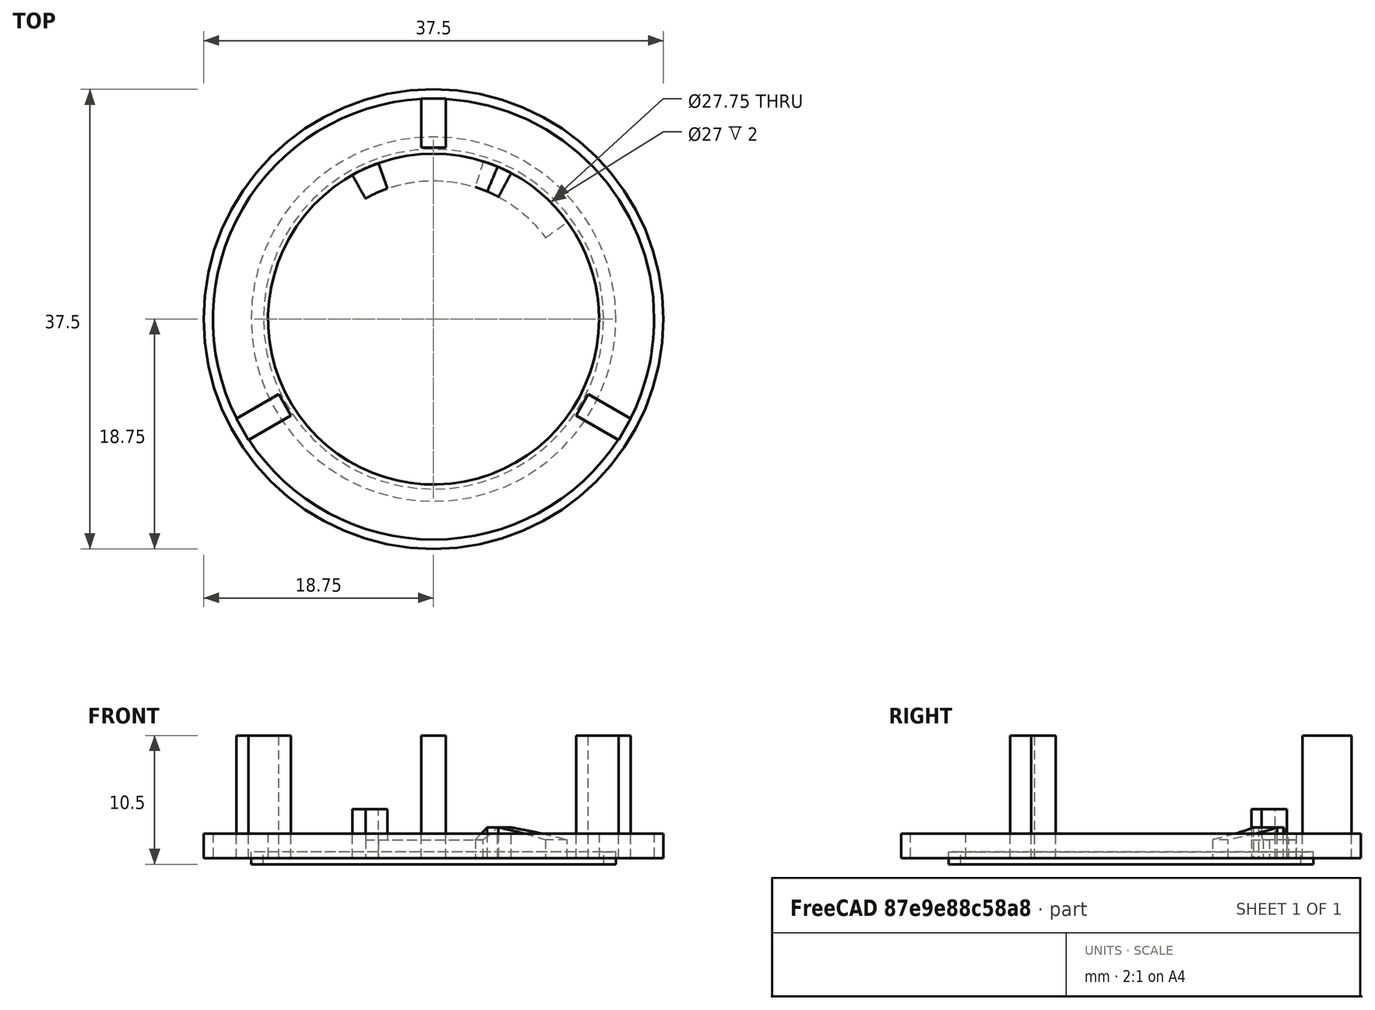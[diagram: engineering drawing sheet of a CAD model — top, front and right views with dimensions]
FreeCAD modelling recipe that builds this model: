
FCSTD DOCUMENT  (FreeCAD 0.19R21857 (Git))
Label: BayonetBaseFemale2
License: All rights reserved
LicenseURL: http://en.wikipedia.org/wiki/All_rights_reserved
objects: Sketcher::SketchObject×28, Part::Sweep×11, Part::MultiFuse×4, Part::Cylinder×3, Part::Mirroring×2, PartDesign::Body×1, Part::Cut×1, Part::Box×1, Part::FeaturePython×1, Image::ImagePlane×1
note: 52 computed .brp shape members not serialized (recipe doc carries the construction recipe); baked Part::Feature solids carry a one-line shape summary decoded from their .brp

FEATURE [Part::Cylinder] Cylinder
  Angle = 360
  AttacherType = Attacher::AttachEngine3D
  Height = 2
  Radius = 18.75
FEATURE [Sketcher::SketchObject] Sketch  label="RampStart"
  Placement = pos=(0,0,0) rot=(1,0,0;1.5708rad)
  sketch-geometry (4):
    g0: LineSegment StartX=-13.5 StartY=0 StartZ=0 EndX=-13.5 EndY=1.5 EndZ=0
    g1: LineSegment StartX=-13.5 StartY=1.5 StartZ=0 EndX=-11.3 EndY=1.5 EndZ=0
    g2: LineSegment StartX=-11.3 StartY=1.5 StartZ=0 EndX=-11.3 EndY=0 EndZ=0
    g3: LineSegment StartX=-11.3 StartY=0 StartZ=0 EndX=-13.5 EndY=0 EndZ=0
  constraints (12):
    c: Coincident(g0,g1)
    c: Coincident(g1,g2)
    c: Coincident(g2,g3)
    c: Coincident(g3,g0)
    c: Parallel(g0,g2)
    c: Parallel(g1,g3)
    c: Horizontal(g3)
    c: Vertical(g2)
    c: DistanceY(g-1,g2) = 0
    c: DistanceX(g2,g-1) = 11.3
    c: DistanceX(g0,g-1) = 13.5
    c: DistanceY(g0,g0) = 1.5
FEATURE [Sketcher::SketchObject] Sketch001  label="InnerCircumference"
  Placement = pos=(0,0,0) rot=(1,0,0;3.14159rad)
  sketch-geometry (1):
    g0: Circle CenterX=0 CenterY=0 CenterZ=0 NormalX=0 NormalY=0 NormalZ=1 AngleXU=0 Radius=11
  constraints (1):
    c: Radius(g0) = 11
FEATURE [Sketcher::SketchObject] Sketch002  label="RampEnd"
  Placement = pos=(0,0,0) rot=(0.950615,-0.219467,-0.219467;1.62142rad)
  sketch-geometry (4):
    g0: LineSegment StartX=-13.5 StartY=0 StartZ=0 EndX=-13.5 EndY=2.5 EndZ=0
    g1: LineSegment StartX=-13.5 StartY=2.5 StartZ=0 EndX=-11.3 EndY=2.5 EndZ=0
    g2: LineSegment StartX=-11.3 StartY=2.5 StartZ=0 EndX=-11.3 EndY=0 EndZ=0
    g3: LineSegment StartX=-11.3 StartY=0 StartZ=0 EndX=-13.5 EndY=0 EndZ=0
  constraints (12):
    c: Coincident(g0,g1)
    c: Coincident(g1,g2)
    c: Coincident(g2,g3)
    c: Coincident(g3,g0)
    c: Parallel(g0,g2)
    c: Parallel(g1,g3)
    c: Horizontal(g3)
    c: Vertical(g2)
    c: DistanceY(g-1,g2) = 0
    c: DistanceX(g2,g-1) = 11.3
    c: DistanceX(g0,g-1) = 13.5
    c: DistanceY(g0,g0) = 2.5
FEATURE [Sketcher::SketchObject] Sketch003  label="RampFlat"
  Placement = pos=(0,0,0) rot=(0.930118,-0.259693,-0.259693;1.64318rad)
  sketch-geometry (4):
    g0: LineSegment StartX=-13.5 StartY=0 StartZ=0 EndX=-13.5 EndY=2.5 EndZ=0
    g1: LineSegment StartX=-13.5 StartY=2.5 StartZ=0 EndX=-11.3 EndY=2.5 EndZ=0
    g2: LineSegment StartX=-11.3 StartY=2.5 StartZ=0 EndX=-11.3 EndY=0 EndZ=0
    g3: LineSegment StartX=-11.3 StartY=0 StartZ=0 EndX=-13.5 EndY=0 EndZ=0
  constraints (12):
    c: Coincident(g0,g1)
    c: Coincident(g1,g2)
    c: Coincident(g2,g3)
    c: Coincident(g3,g0)
    c: Parallel(g0,g2)
    c: Parallel(g1,g3)
    c: Horizontal(g3)
    c: Vertical(g2)
    c: DistanceY(g-1,g2) = 0
    c: DistanceX(g2,g-1) = 11.3
    c: DistanceX(g0,g-1) = 13.5
    c: DistanceY(g0,g0) = 2.5
FEATURE [Sketcher::SketchObject] Sketch004  label="LockFlat"
  Placement = pos=(0,0,0) rot=(0.906297,-0.298852,-0.298852;1.66903rad)
  sketch-geometry (4):
    g0: LineSegment StartX=-13.5 StartY=0 StartZ=0 EndX=-13.5 EndY=1.5 EndZ=0
    g1: LineSegment StartX=-13.5 StartY=1.5 StartZ=0 EndX=-11.3 EndY=1.5 EndZ=0
    g2: LineSegment StartX=-11.3 StartY=1.5 StartZ=0 EndX=-11.3 EndY=0 EndZ=0
    g3: LineSegment StartX=-11.3 StartY=0 StartZ=0 EndX=-13.5 EndY=0 EndZ=0
  constraints (12):
    c: Coincident(g0,g1)
    c: Coincident(g1,g2)
    c: Coincident(g2,g3)
    c: Coincident(g3,g0)
    c: Parallel(g0,g2)
    c: Parallel(g1,g3)
    c: Horizontal(g3)
    c: Vertical(g2)
    c: DistanceY(g-1,g2) = 0
    c: DistanceX(g2,g-1) = 11.3
    c: DistanceX(g0,g-1) = 13.5
    c: DistanceY(g0,g0) = 1.5
FEATURE [Sketcher::SketchObject] Sketch005  label="LockFlatEnd"
  Placement = pos=(0,0,0) rot=(0.621652,-0.553872,-0.553872;2.02922rad)
  sketch-geometry (4):
    g0: LineSegment StartX=-13.5 StartY=0 StartZ=0 EndX=-13.5 EndY=1.5 EndZ=0
    g1: LineSegment StartX=-13.5 StartY=1.5 StartZ=0 EndX=-11.3 EndY=1.5 EndZ=0
    g2: LineSegment StartX=-11.3 StartY=1.5 StartZ=0 EndX=-11.3 EndY=0 EndZ=0
    g3: LineSegment StartX=-11.3 StartY=0 StartZ=0 EndX=-13.5 EndY=0 EndZ=0
  constraints (12):
    c: Coincident(g0,g1)
    c: Coincident(g1,g2)
    c: Coincident(g2,g3)
    c: Coincident(g3,g0)
    c: Parallel(g0,g2)
    c: Parallel(g1,g3)
    c: Horizontal(g3)
    c: Vertical(g2)
    c: DistanceY(g-1,g2) = 0
    c: DistanceX(g2,g-1) = 11.3
    c: DistanceX(g0,g-1) = 13.5
    c: DistanceY(g0,g0) = 1.5
FEATURE [Sketcher::SketchObject] Sketch006  label="RampPath"
  sketch-geometry (1):
    g0: ArcOfCircle CenterX=0 CenterY=0 CenterZ=0 NormalX=0 NormalY=0 NormalZ=1 AngleXU=0 Radius=11.0109 StartAngle=1.68589 EndAngle=3.14182
FEATURE [Sketcher::SketchObject] Sketch007  label="Path1"
  sketch-geometry (2):
    g0: ArcOfCircle CenterX=0 CenterY=0 CenterZ=0 NormalX=0 NormalY=0 NormalZ=1 AngleXU=0 Radius=11.3 StartAngle=2.68754 EndAngle=3.14132
    g1: GeomPoint X=-10.1564 Y=4.95359 Z=0
  constraints (3):
    c: Radius(g0) = 11.3
    c: Coincident(g-1,g0)
    c: Angle(g0) = 0.453786
FEATURE [PartDesign::Body] Body
  Group = -> [Sketch005,Sketch004,Sketch003,Sketch002,Sketch001,Sketch,Sketch006,Sketch007]
  Origin = -> Origin
FEATURE [Part::Sweep] Sweep
  Frenet = false
  Sections = -> [Sketch,Sketch002]
  Solid = true
  Spine = -> Sketch007 [Edge1]
  Transition = 1
FEATURE [Sketcher::SketchObject] Sketch008  label="Path2"
  sketch-geometry (1):
    g0: ArcOfCircle CenterX=0 CenterY=0 CenterZ=0 NormalX=0 NormalY=0 NormalZ=1 AngleXU=0 Radius=11.3 StartAngle=2.59707 EndAngle=2.68754
  constraints (2):
    c: Radius(g0) = 11.3
    c: Coincident(g0,g-1)
FEATURE [Sketcher::SketchObject] Sketch009  label="Path3"
  sketch-geometry (1):
    g0: ArcOfCircle CenterX=0 CenterY=0 CenterZ=0 NormalX=0 NormalY=0 NormalZ=1 AngleXU=0 Radius=11.3 StartAngle=2.50468 EndAngle=2.59704
  constraints (2):
    c: Radius(g0) = 11.3
    c: Coincident(g0,g-1)
FEATURE [Sketcher::SketchObject] Sketch010  label="Path4"
  sketch-geometry (1):
    g0: ArcOfCircle CenterX=0 CenterY=0 CenterZ=0 NormalX=0 NormalY=0 NormalZ=1 AngleXU=0 Radius=11.3 StartAngle=1.68594 EndAngle=2.50452
  constraints (2):
    c: Radius(g0) = 11.3
    c: Coincident(g0,g-1)
FEATURE [Part::Sweep] Sweep001
  Frenet = false
  Sections = -> [Sketch002,Sketch003]
  Solid = true
  Spine = -> Sketch008 [Edge1]
  Transition = 1
FEATURE [Part::Sweep] Sweep002
  Frenet = false
  Sections = -> [Sketch003,Sketch004]
  Solid = true
  Spine = -> Sketch009 [Edge1]
  Transition = 1
FEATURE [Part::Sweep] Sweep003
  Frenet = false
  Sections = -> [Sketch004,Sketch005]
  Solid = true
  Spine = -> Sketch010 [Edge1]
  Transition = 1
FEATURE [Part::MultiFuse] Fusion  label="Ramp"
  Shapes = -> [Sweep,Sweep001,Sweep002,Sweep003]
FEATURE [Sketcher::SketchObject] Sketch011  label="EndstopEnd"
  Placement = pos=(0,0,0) rot=(0.621652,-0.553872,-0.553872;2.02922rad)
  sketch-geometry (4):
    g0: LineSegment StartX=-13.5 StartY=0 StartZ=0 EndX=-13.5 EndY=4 EndZ=0
    g1: LineSegment StartX=-13.5 StartY=4 StartZ=0 EndX=-11.3 EndY=4 EndZ=0
    g2: LineSegment StartX=-11.3 StartY=4 StartZ=0 EndX=-11.3 EndY=0 EndZ=0
    g3: LineSegment StartX=-11.3 StartY=0 StartZ=0 EndX=-13.5 EndY=0 EndZ=0
  constraints (12):
    c: Coincident(g0,g1)
    c: Coincident(g1,g2)
    c: Coincident(g2,g3)
    c: Coincident(g3,g0)
    c: Parallel(g0,g2)
    c: Parallel(g1,g3)
    c: Horizontal(g3)
    c: Vertical(g2)
    c: DistanceY(g-1,g2) = 0
    c: DistanceX(g2,g-1) = 11.3
    c: DistanceX(g0,g-1) = 13.5
    c: DistanceY(g0,g0) = 4
FEATURE [Sketcher::SketchObject] Sketch012  label="EndstopStart"
  Placement = pos=(0,0,0) rot=(0.688237,-0.512996,-0.512996;1.93602rad)
  sketch-geometry (4):
    g0: LineSegment StartX=-13.5 StartY=0 StartZ=0 EndX=-13.5 EndY=4 EndZ=0
    g1: LineSegment StartX=-13.5 StartY=4 StartZ=0 EndX=-11.3 EndY=4 EndZ=0
    g2: LineSegment StartX=-11.3 StartY=4 StartZ=0 EndX=-11.3 EndY=0 EndZ=0
    g3: LineSegment StartX=-11.3 StartY=0 StartZ=0 EndX=-13.5 EndY=0 EndZ=0
  constraints (12):
    c: Coincident(g0,g1)
    c: Coincident(g1,g2)
    c: Coincident(g2,g3)
    c: Coincident(g3,g0)
    c: Parallel(g0,g2)
    c: Parallel(g1,g3)
    c: Horizontal(g3)
    c: Vertical(g2)
    c: DistanceY(g-1,g2) = 0
    c: DistanceX(g2,g-1) = 11.3
    c: DistanceX(g0,g-1) = 13.5
    c: DistanceY(g0,g0) = 4
FEATURE [Sketcher::SketchObject] Sketch013  label="EndstopPath"
  sketch-geometry (1):
    g0: ArcOfCircle CenterX=0 CenterY=0 CenterZ=0 NormalX=0 NormalY=0 NormalZ=1 AngleXU=0 Radius=11.3 StartAngle=1.68607 EndAngle=1.86043
  constraints (2):
    c: Radius(g0) = 11.3
    c: Coincident(g-1,g0)
FEATURE [Part::Sweep] Sweep004  label="EndStop"
  Frenet = false
  Sections = -> [Sketch012,Sketch011]
  Solid = true
  Spine = -> Sketch013 [Edge1]
  Transition = 1
FEATURE [Part::MultiFuse] Fusion001  label="RampWithEndstop"
  Shapes = -> [Fusion,Sweep004]
FEATURE [Part::Cylinder] Cylinder001
  Angle = 360
  AttacherType = Attacher::AttachEngine3D
  Height = 2
  Radius = 18
FEATURE [Part::Cylinder] Cylinder002
  Angle = 360
  AttacherType = Attacher::AttachEngine3D
  Height = 2
  Radius = 13.5
FEATURE [Part::Cut] Cut  label="Base"
  Base = -> Cylinder001
  Placement = pos=(0,0,2) rot=(1,0,0;3.14159rad)
  Tool = -> Cylinder002
FEATURE [Sketcher::SketchObject] Sketch015  label="GrooveProfile"
  Placement = pos=(0,0,0) rot=(1,0,0;1.5708rad)
  sketch-geometry (4):
    g0: LineSegment StartX=-14.875 StartY=-0.5 StartZ=0 EndX=-13.875 EndY=-0.5 EndZ=0
    g1: LineSegment StartX=-13.875 StartY=-0.5 StartZ=0 EndX=-13.875 EndY=0.5 EndZ=0
    g2: LineSegment StartX=-13.875 StartY=0.5 StartZ=0 EndX=-14.875 EndY=0.5 EndZ=0
    g3: LineSegment StartX=-14.875 StartY=0.5 StartZ=0 EndX=-14.875 EndY=-0.5 EndZ=0
  constraints (12):
    c: Coincident(g0,g1)
    c: Coincident(g1,g2)
    c: Coincident(g2,g3)
    c: Coincident(g3,g0)
    c: Horizontal(g0)
    c: Horizontal(g2)
    c: Vertical(g1)
    c: Vertical(g3)
    c: DistanceX(g0,g0) = 1
    c: Equal(g0,g1)
    c: DistanceY(g1,g-1) = -0.5
    c: DistanceX(g1,g-1) = 13.875
FEATURE [Sketcher::SketchObject] Sketch016  label="GroovePath"
  sketch-geometry (1):
    g0: Circle CenterX=0 CenterY=0 CenterZ=0 NormalX=0 NormalY=0 NormalZ=1 AngleXU=0 Radius=13.875
  constraints (2):
    c: Coincident(g0,g-1)
    c: Radius(g0) = 13.875
FEATURE [Part::Sweep] Sweep005  label="Groove"
  Frenet = false
  Sections = -> [Sketch015]
  Solid = true
  Spine = -> Sketch016 [Edge1]
  Transition = 1
FEATURE [Part::Box] Box  label="Cube"
  AttacherType = Attacher::AttachEngine3D
  Height = 10
  Length = 2
  Placement = pos=(-1,14,0) rot=(0,0,1;0rad)
  Width = 4
FEATURE [Part::FeaturePython] Array001  label="Testhandles"  # Draft array (typed FeaturePython)
  Angle = 360
  ArrayType = 1
  Axis = (0,0,1)
  Base = -> Box
  Center = (0,0,0)
  Fuse = false
  IntervalAxis = (0,0,0)
  IntervalX = (1,0,0)
  IntervalY = (0,1,0)
  IntervalZ = (0,0,1)
  NumberPolar = 3
  NumberX = 0
  NumberY = 0
  NumberZ = 0
FEATURE [Part::Mirroring] Part__Mirroring  label="RampWithEndstop (Mirror #1)"
  Base = (0,0,0)
  Normal = (0,1,0)
  Placement = pos=(0,0,0) rot=(0,0,-1;2.51327rad)
  Source = -> Fusion001
FEATURE [Image::ImagePlane] ImagePlane
  Placement = pos=(0.5,6,2) rot=(0,1,0;3.14159rad)
  XSize = 50.7829
  YSize = 59.8109
FEATURE [Sketcher::SketchObject] Sketch017  label="RampEnd001"
  Placement = pos=(0,0,0) rot=(0.950615,-0.219467,-0.219467;1.62142rad)
  sketch-geometry (4):
    g0: LineSegment StartX=-13.5 StartY=0 StartZ=0 EndX=-13.5 EndY=2.5 EndZ=0
    g1: LineSegment StartX=-13.5 StartY=2.5 StartZ=0 EndX=-11.3 EndY=2.5 EndZ=0
    g2: LineSegment StartX=-11.3 StartY=2.5 StartZ=0 EndX=-11.3 EndY=0 EndZ=0
    g3: LineSegment StartX=-11.3 StartY=0 StartZ=0 EndX=-13.5 EndY=0 EndZ=0
  constraints (12):
    c: Coincident(g0,g1)
    c: Coincident(g1,g2)
    c: Coincident(g2,g3)
    c: Coincident(g3,g0)
    c: Parallel(g0,g2)
    c: Parallel(g1,g3)
    c: Horizontal(g3)
    c: Vertical(g2)
    c: DistanceY(g-1,g2) = 0
    c: DistanceX(g2,g-1) = 11.3
    c: DistanceX(g0,g-1) = 13.5
    c: DistanceY(g0,g0) = 2.5
FEATURE [Sketcher::SketchObject] Sketch018  label="RampFlat001"
  Placement = pos=(0,0,0) rot=(0.930118,-0.259693,-0.259693;1.64318rad)
  sketch-geometry (4):
    g0: LineSegment StartX=-13.5 StartY=0 StartZ=0 EndX=-13.5 EndY=2.5 EndZ=0
    g1: LineSegment StartX=-13.5 StartY=2.5 StartZ=0 EndX=-11.3 EndY=2.5 EndZ=0
    g2: LineSegment StartX=-11.3 StartY=2.5 StartZ=0 EndX=-11.3 EndY=0 EndZ=0
    g3: LineSegment StartX=-11.3 StartY=0 StartZ=0 EndX=-13.5 EndY=0 EndZ=0
  constraints (12):
    c: Coincident(g0,g1)
    c: Coincident(g1,g2)
    c: Coincident(g2,g3)
    c: Coincident(g3,g0)
    c: Parallel(g0,g2)
    c: Parallel(g1,g3)
    c: Horizontal(g3)
    c: Vertical(g2)
    c: DistanceY(g-1,g2) = 0
    c: DistanceX(g2,g-1) = 11.3
    c: DistanceX(g0,g-1) = 13.5
    c: DistanceY(g0,g0) = 2.5
FEATURE [Sketcher::SketchObject] Sketch019  label="LockFlat001"
  Placement = pos=(0,0,0) rot=(0.906297,-0.298852,-0.298852;1.66903rad)
  sketch-geometry (4):
    g0: LineSegment StartX=-13.5 StartY=0 StartZ=0 EndX=-13.5 EndY=1.5 EndZ=0
    g1: LineSegment StartX=-13.5 StartY=1.5 StartZ=0 EndX=-11.3 EndY=1.5 EndZ=0
    g2: LineSegment StartX=-11.3 StartY=1.5 StartZ=0 EndX=-11.3 EndY=0 EndZ=0
    g3: LineSegment StartX=-11.3 StartY=0 StartZ=0 EndX=-13.5 EndY=0 EndZ=0
  constraints (12):
    c: Coincident(g0,g1)
    c: Coincident(g1,g2)
    c: Coincident(g2,g3)
    c: Coincident(g3,g0)
    c: Parallel(g0,g2)
    c: Parallel(g1,g3)
    c: Horizontal(g3)
    c: Vertical(g2)
    c: DistanceY(g-1,g2) = 0
    c: DistanceX(g2,g-1) = 11.3
    c: DistanceX(g0,g-1) = 13.5
    c: DistanceY(g0,g0) = 1.5
FEATURE [Sketcher::SketchObject] Sketch020  label="LockFlatEnd001"
  Placement = pos=(0,0,0) rot=(0.621652,-0.553872,-0.553872;2.02922rad)
  sketch-geometry (4):
    g0: LineSegment StartX=-13.5 StartY=0 StartZ=0 EndX=-13.5 EndY=1.5 EndZ=0
    g1: LineSegment StartX=-13.5 StartY=1.5 StartZ=0 EndX=-11.3 EndY=1.5 EndZ=0
    g2: LineSegment StartX=-11.3 StartY=1.5 StartZ=0 EndX=-11.3 EndY=0 EndZ=0
    g3: LineSegment StartX=-11.3 StartY=0 StartZ=0 EndX=-13.5 EndY=0 EndZ=0
  constraints (12):
    c: Coincident(g0,g1)
    c: Coincident(g1,g2)
    c: Coincident(g2,g3)
    c: Coincident(g3,g0)
    c: Parallel(g0,g2)
    c: Parallel(g1,g3)
    c: Horizontal(g3)
    c: Vertical(g2)
    c: DistanceY(g-1,g2) = 0
    c: DistanceX(g2,g-1) = 11.3
    c: DistanceX(g0,g-1) = 13.5
    c: DistanceY(g0,g0) = 1.5
FEATURE [Sketcher::SketchObject] Sketch021  label="Path005"
  sketch-geometry (2):
    g0: ArcOfCircle CenterX=0 CenterY=0 CenterZ=0 NormalX=0 NormalY=0 NormalZ=1 AngleXU=0 Radius=11.3 StartAngle=2.68754 EndAngle=3.14132
    g1: GeomPoint X=-10.1564 Y=4.95359 Z=0
  constraints (3):
    c: Radius(g0) = 11.3
    c: Coincident(g-1,g0)
    c: Angle(g0) = 0.453786
FEATURE [Sketcher::SketchObject] Sketch022  label="Path006"
  sketch-geometry (1):
    g0: ArcOfCircle CenterX=0 CenterY=0 CenterZ=0 NormalX=0 NormalY=0 NormalZ=1 AngleXU=0 Radius=11.3 StartAngle=2.59707 EndAngle=2.68754
  constraints (2):
    c: Radius(g0) = 11.3
    c: Coincident(g0,g-1)
FEATURE [Part::Sweep] Sweep007
  Frenet = false
  Sections = -> [Sketch017,Sketch018]
  Solid = true
  Spine = -> Sketch022 [Edge1]
  Transition = 1
FEATURE [Sketcher::SketchObject] Sketch023  label="Path007"
  sketch-geometry (1):
    g0: ArcOfCircle CenterX=0 CenterY=0 CenterZ=0 NormalX=0 NormalY=0 NormalZ=1 AngleXU=0 Radius=11.3 StartAngle=2.50468 EndAngle=2.59704
  constraints (2):
    c: Radius(g0) = 11.3
    c: Coincident(g0,g-1)
FEATURE [Part::Sweep] Sweep006
  Frenet = false
  Sections = -> [Sketch018,Sketch019]
  Solid = true
  Spine = -> Sketch023 [Edge1]
  Transition = 1
FEATURE [Sketcher::SketchObject] Sketch024  label="Path008"
  sketch-geometry (1):
    g0: ArcOfCircle CenterX=0 CenterY=0 CenterZ=0 NormalX=0 NormalY=0 NormalZ=1 AngleXU=0 Radius=11.3 StartAngle=1.68594 EndAngle=2.50452
  constraints (2):
    c: Radius(g0) = 11.3
    c: Coincident(g0,g-1)
FEATURE [Sketcher::SketchObject] Sketch025  label="EndstopEnd001"
  Placement = pos=(0,0,0) rot=(0.621652,-0.553872,-0.553872;2.02922rad)
  sketch-geometry (4):
    g0: LineSegment StartX=-13.5 StartY=0 StartZ=0 EndX=-13.5 EndY=4 EndZ=0
    g1: LineSegment StartX=-13.5 StartY=4 StartZ=0 EndX=-11.3 EndY=4 EndZ=0
    g2: LineSegment StartX=-11.3 StartY=4 StartZ=0 EndX=-11.3 EndY=0 EndZ=0
    g3: LineSegment StartX=-11.3 StartY=0 StartZ=0 EndX=-13.5 EndY=0 EndZ=0
  constraints (12):
    c: Coincident(g0,g1)
    c: Coincident(g1,g2)
    c: Coincident(g2,g3)
    c: Coincident(g3,g0)
    c: Parallel(g0,g2)
    c: Parallel(g1,g3)
    c: Horizontal(g3)
    c: Vertical(g2)
    c: DistanceY(g-1,g2) = 0
    c: DistanceX(g2,g-1) = 11.3
    c: DistanceX(g0,g-1) = 13.5
    c: DistanceY(g0,g0) = 4
FEATURE [Sketcher::SketchObject] Sketch026  label="EndstopStart001"
  Placement = pos=(0,0,0) rot=(0.688237,-0.512996,-0.512996;1.93602rad)
  sketch-geometry (4):
    g0: LineSegment StartX=-13.5 StartY=0 StartZ=0 EndX=-13.5 EndY=4 EndZ=0
    g1: LineSegment StartX=-13.5 StartY=4 StartZ=0 EndX=-11.3 EndY=4 EndZ=0
    g2: LineSegment StartX=-11.3 StartY=4 StartZ=0 EndX=-11.3 EndY=0 EndZ=0
    g3: LineSegment StartX=-11.3 StartY=0 StartZ=0 EndX=-13.5 EndY=0 EndZ=0
  constraints (12):
    c: Coincident(g0,g1)
    c: Coincident(g1,g2)
    c: Coincident(g2,g3)
    c: Coincident(g3,g0)
    c: Parallel(g0,g2)
    c: Parallel(g1,g3)
    c: Horizontal(g3)
    c: Vertical(g2)
    c: DistanceY(g-1,g2) = 0
    c: DistanceX(g2,g-1) = 11.3
    c: DistanceX(g0,g-1) = 13.5
    c: DistanceY(g0,g0) = 4
FEATURE [Sketcher::SketchObject] Sketch027  label="EndstopPath001"
  sketch-geometry (1):
    g0: ArcOfCircle CenterX=0 CenterY=0 CenterZ=0 NormalX=0 NormalY=0 NormalZ=1 AngleXU=0 Radius=11.3 StartAngle=1.68607 EndAngle=1.86043
  constraints (2):
    c: Radius(g0) = 11.3
    c: Coincident(g-1,g0)
FEATURE [Part::Sweep] Sweep009  label="EndStop001"
  Frenet = false
  Sections = -> [Sketch026,Sketch025]
  Solid = true
  Spine = -> Sketch027 [Edge1]
  Transition = 1
FEATURE [Part::Sweep] Sweep010
  Frenet = false
  Sections = -> [Sketch019,Sketch020]
  Solid = true
  Spine = -> Sketch024 [Edge1]
  Transition = 1
FEATURE [Sketcher::SketchObject] Sketch028  label="RampStart001"
  Placement = pos=(0,0,0) rot=(1,0,0;1.5708rad)
  sketch-geometry (4):
    g0: LineSegment StartX=-13.5 StartY=0 StartZ=0 EndX=-13.5 EndY=1.5 EndZ=0
    g1: LineSegment StartX=-13.5 StartY=1.5 StartZ=0 EndX=-11.3 EndY=1.5 EndZ=0
    g2: LineSegment StartX=-11.3 StartY=1.5 StartZ=0 EndX=-11.3 EndY=0 EndZ=0
    g3: LineSegment StartX=-11.3 StartY=0 StartZ=0 EndX=-13.5 EndY=0 EndZ=0
  constraints (12):
    c: Coincident(g0,g1)
    c: Coincident(g1,g2)
    c: Coincident(g2,g3)
    c: Coincident(g3,g0)
    c: Parallel(g0,g2)
    c: Parallel(g1,g3)
    c: Horizontal(g3)
    c: Vertical(g2)
    c: DistanceY(g-1,g2) = 0
    c: DistanceX(g2,g-1) = 11.3
    c: DistanceX(g0,g-1) = 13.5
    c: DistanceY(g0,g0) = 1.5
FEATURE [Part::Sweep] Sweep008
  Frenet = false
  Sections = -> [Sketch028,Sketch017]
  Solid = true
  Spine = -> Sketch021 [Edge1]
  Transition = 1
FEATURE [Part::MultiFuse] Fusion002  label="Ramp001"
  Shapes = -> [Sweep008,Sweep007,Sweep006,Sweep010]
FEATURE [Part::MultiFuse] Fusion003  label="RampWithEndstop001"
  Shapes = -> [Fusion002,Sweep009]
FEATURE [Part::Mirroring] Part__Mirroring001  label="RampWithEndstopShort1"
  Base = (0,0,0)
  Normal = (0,1,0)
  Placement = pos=(0,0,0) rot=(0,0,1;3.76991rad)
  Source = -> Fusion003
